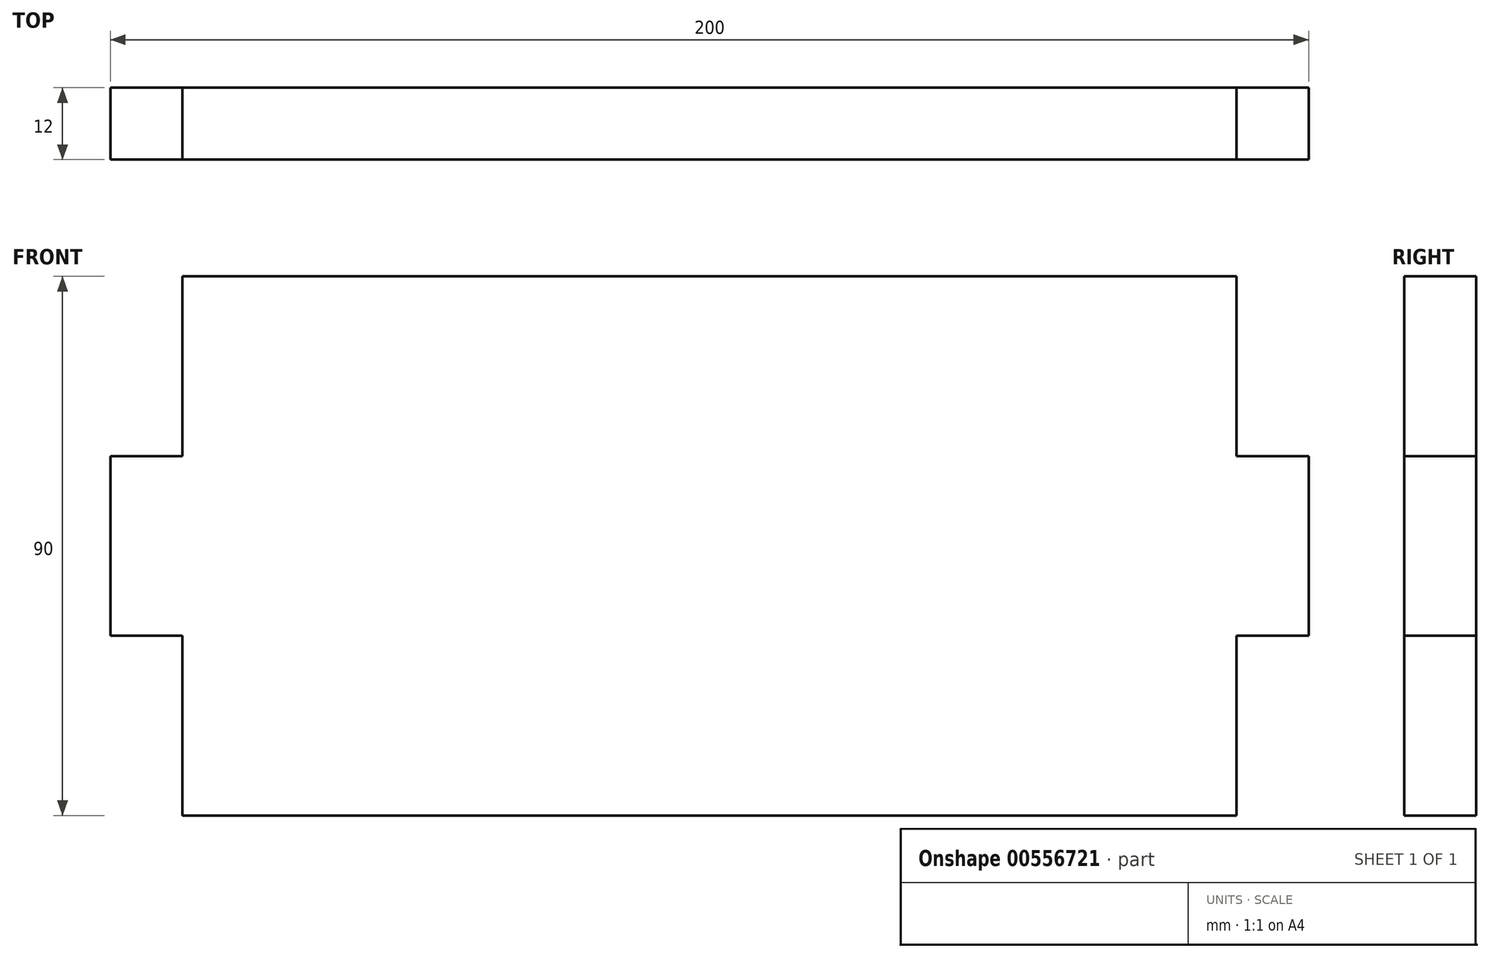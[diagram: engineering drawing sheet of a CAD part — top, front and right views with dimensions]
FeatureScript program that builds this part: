
annotation { "Feature Type Name" : "Feature", "Feature Type Description" : "" }
export const myFeature = defineFeature(function(context is Context, id is Id, definition is map)
    precondition{}
    {
        {
            var Q0;
            Q0=qCreatedBy(makeId("Front.planeOp"),FACE);
            var sketch = newSketch(context, id + "F0", { "sketchPlane" : qUnion([Q0])});
            skLineSegment(sketch, "E0", {"start": v(0, 0) * mm, "end": v(0, 30) * mm});
            skLineSegment(sketch, "E1", {"start": v(0, 30) * mm, "end": v(12, 30) * mm});
            skLineSegment(sketch, "E2", {"start": v(12, 30) * mm, "end": v(12, 60) * mm});
            skLineSegment(sketch, "E3", {"start": v(12, 60) * mm, "end": v(0, 60) * mm});
            skLineSegment(sketch, "E4", {"start": v(0, 60) * mm, "end": v(0, 90) * mm});
            skLineSegment(sketch, "E5", {"start": v(0, 90) * mm, "end": v(-88, 90) * mm});
            skLineSegment(sketch, "E6", {"start": v(-88, 90) * mm, "end": v(-88, 0) * mm, "construction": true});
            skLineSegment(sketch, "E7", {"start": v(-88, 0) * mm, "end": v(0, 0) * mm});
            skLineSegment(sketch, "E8.MirrorCS", {"start": v(-176, 0) * mm, "end": v(-176, 30) * mm});
            skLineSegment(sketch, "E9.MirrorCS", {"start": v(-176, 90) * mm, "end": v(-88, 90) * mm});
            skLineSegment(sketch, "E10.MirrorCS", {"start": v(-88, 0) * mm, "end": v(-176, 0) * mm});
            skLineSegment(sketch, "E11.MirrorCS", {"start": v(-188, 60) * mm, "end": v(-176, 60) * mm});
            skLineSegment(sketch, "E12.MirrorCS", {"start": v(-176, 30) * mm, "end": v(-188, 30) * mm});
            skLineSegment(sketch, "E13.MirrorCS", {"start": v(-188, 30) * mm, "end": v(-188, 60) * mm});
            skLineSegment(sketch, "E14.MirrorCS", {"start": v(-176, 60) * mm, "end": v(-176, 90) * mm});
            skSolve(sketch);
        }
        {
            var Q0;
            Q0=makeQuery(id+"F0.imprint","IMPRINT",FACE,{"disambiguationData":[TD([[makeQuery(id+"F0.imprint","IMPRINT",EDGE,{"derivedFrom":sQuery(id+"F0.wireOp",EDGE,"E0")}),1.0]])]});
            extrude(context, id + "F1", {"entities" : qUnion([Q0]), "endBound" : BoundingType.SYMMETRIC, "depth" : 12 * mm, "offsetDistance" : 25 * mm});
        }
    });
